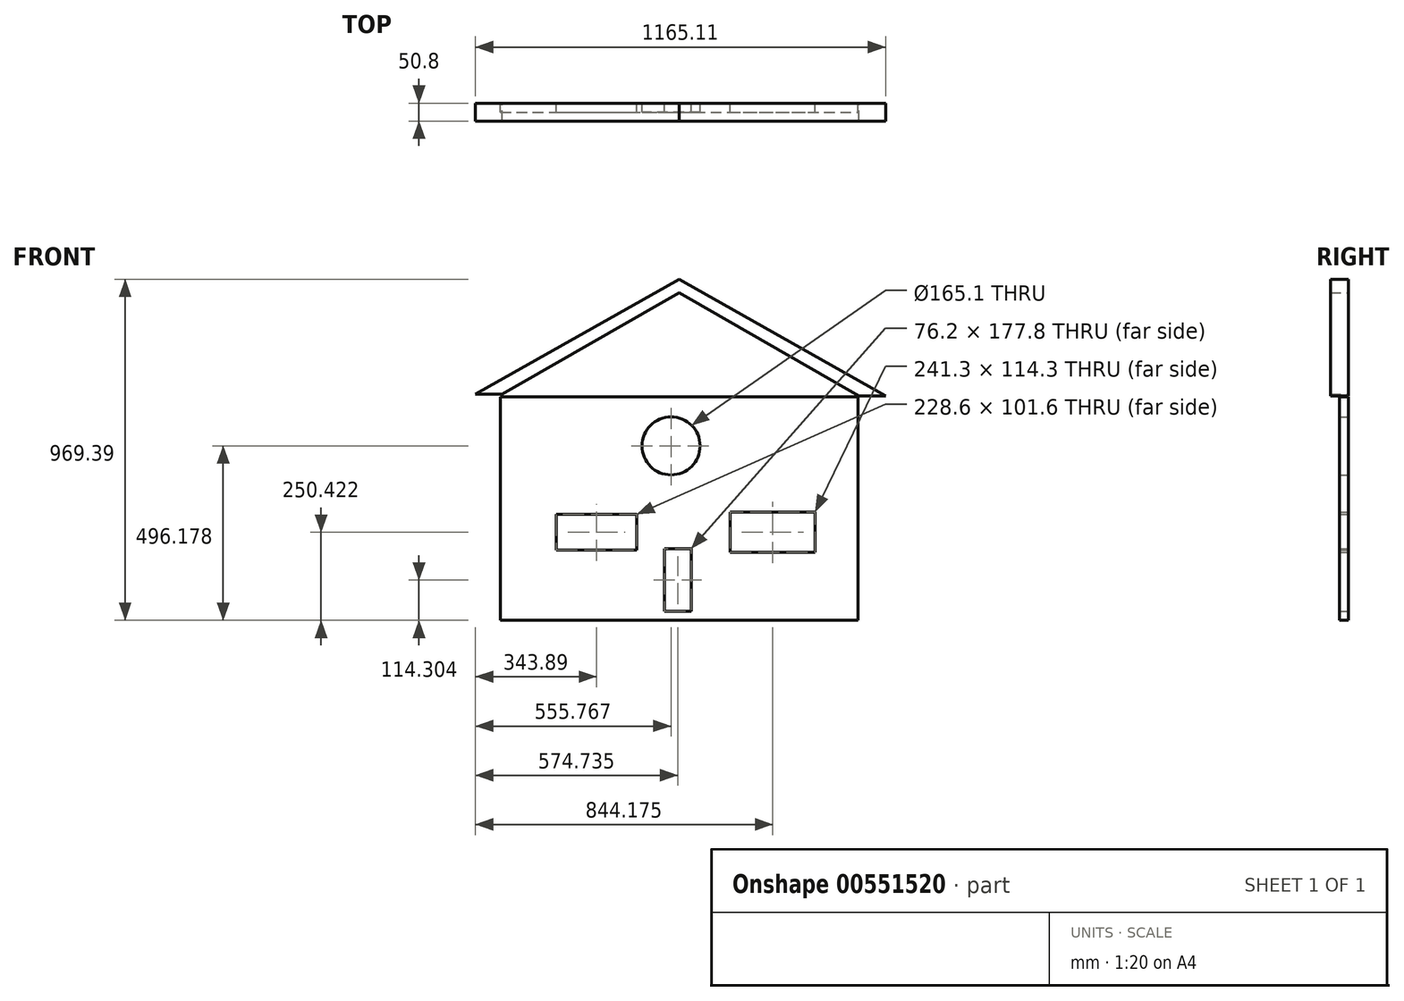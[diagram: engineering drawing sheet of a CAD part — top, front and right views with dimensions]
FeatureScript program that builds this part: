
annotation { "Feature Type Name" : "Feature", "Feature Type Description" : "" }
export const myFeature = defineFeature(function(context is Context, id is Id, definition is map)
    precondition{}
    {
        {
            var Q0;
            Q0=qCreatedBy(makeId("Front.planeOp"),FACE);
            var sketch = newSketch(context, id + "F0", { "sketchPlane" : qUnion([Q0])});
            skLineSegment(sketch, "E0", {"start": v(-620.3, -141.94) * mm, "end": v(-112.3, -141.94) * mm});
            skLineSegment(sketch, "E1", {"start": v(-112.3, -141.94) * mm, "end": v(395.7, -141.94) * mm});
            skLineSegment(sketch, "E2", {"start": v(-112.3, -99.65) * mm, "end": v(-112.3, 154.35) * mm, "construction": true});
            skLineSegment(sketch, "E3", {"start": v(-614.94, -133.46) * mm, "end": v(-112.3, 154.35) * mm});
            skLineSegment(sketch, "E4", {"start": v(397.77, -138.3) * mm, "end": v(-112.3, 154.35) * mm});
            skLineSegment(sketch, "E5", {"start": v(397.77, -138.3) * mm, "end": v(473.97, -138.3) * mm});
            skLineSegment(sketch, "E6", {"start": v(-614.94, -133.46) * mm, "end": v(-691.14, -133.46) * mm});
            skLineSegment(sketch, "E7", {"start": v(-112.3, 154.35) * mm, "end": v(-112.3, 192.45) * mm});
            skLineSegment(sketch, "E8", {"start": v(-691.14, -133.46) * mm, "end": v(-112.3, 192.45) * mm});
            skLineSegment(sketch, "E9", {"start": v(473.97, -138.3) * mm, "end": v(-112.3, 192.45) * mm});
            skLineSegment(sketch, "E10", {"start": v(-620.3, -141.94) * mm, "end": v(-620.3, -751.54) * mm});
            skLineSegment(sketch, "E11", {"start": v(-620.3, -751.54) * mm, "end": v(395.7, -751.54) * mm});
            skLineSegment(sketch, "E12", {"start": v(395.7, -751.54) * mm, "end": v(395.7, -141.94) * mm});
            skLineSegment(sketch, "E13", {"start": v(-620.3, -751.54) * mm, "end": v(-620.3, -776.94) * mm});
            skLineSegment(sketch, "E14", {"start": v(395.7, -751.54) * mm, "end": v(395.7, -776.94) * mm});
            skLineSegment(sketch, "E15", {"start": v(-620.3, -776.94) * mm, "end": v(395.7, -776.94) * mm});
            skLineSegment(sketch, "E16", {"start": v(-154.5, -751.54) * mm, "end": v(-154.5, -573.74) * mm});
            skLineSegment(sketch, "E17", {"start": v(-154.5, -573.74) * mm, "end": v(-78.3, -573.74) * mm});
            skLineSegment(sketch, "E18", {"start": v(-78.3, -573.74) * mm, "end": v(-78.3, -751.54) * mm});
            skLineSegment(sketch, "E19.bottom", {"start": v(-461.55, -475.72) * mm, "end": v(-232.95, -475.72) * mm});
            skLineSegment(sketch, "E19.top", {"start": v(-461.55, -577.32) * mm, "end": v(-232.95, -577.32) * mm});
            skLineSegment(sketch, "E19.left", {"start": v(-461.55, -475.72) * mm, "end": v(-461.55, -577.32) * mm});
            skLineSegment(sketch, "E19.right", {"start": v(-232.95, -475.72) * mm, "end": v(-232.95, -577.32) * mm});
            skLineSegment(sketch, "E20.bottom", {"start": v(38.73, -475.72) * mm, "end": v(267.33, -475.72) * mm});
            skLineSegment(sketch, "E20.top", {"start": v(38.73, -577.32) * mm, "end": v(267.33, -577.32) * mm});
            skLineSegment(sketch, "E20.left", {"start": v(38.73, -475.72) * mm, "end": v(38.73, -577.32) * mm});
            skLineSegment(sketch, "E20.right", {"start": v(267.33, -475.72) * mm, "end": v(267.33, -577.32) * mm});
            skCircle(sketch, "E21", {"center": v(-135.37, -280.76) * mm, "radius": 76.2 * mm});
            skCircle(sketch, "E22.0", {"center": v(-135.37, -280.76) * mm, "radius": 82.55 * mm});
            skLineSegment(sketch, "E23.0", {"start": v(-457.53, -479.74) * mm, "end": v(-236.97, -479.74) * mm});
            skLineSegment(sketch, "E23.1", {"start": v(-457.53, -479.74) * mm, "end": v(-457.53, -573.3) * mm});
            skLineSegment(sketch, "E23.2", {"start": v(-457.53, -573.3) * mm, "end": v(-236.97, -573.3) * mm});
            skLineSegment(sketch, "E23.3", {"start": v(-236.97, -479.74) * mm, "end": v(-236.97, -573.3) * mm});
            skLineSegment(sketch, "E24.0", {"start": v(32.38, -583.67) * mm, "end": v(273.68, -583.67) * mm});
            skLineSegment(sketch, "E24.1", {"start": v(32.38, -469.37) * mm, "end": v(32.38, -583.67) * mm});
            skLineSegment(sketch, "E24.2", {"start": v(32.38, -469.37) * mm, "end": v(273.68, -469.37) * mm});
            skLineSegment(sketch, "E24.3", {"start": v(273.68, -469.37) * mm, "end": v(273.68, -583.67) * mm});
            skSolve(sketch);
        }
        {
            var Q0;
            Q0=makeQuery(id+"F0.imprint","IMPRINT",FACE,{"disambiguationData":[TD([[makeQuery(id+"F0.imprint","IMPRINT",EDGE,{"derivedFrom":sQuery(id+"F0.wireOp",EDGE,"E3")}),1.0]])]});
            var Q1;
            Q1=makeQuery(id+"F0.imprint","IMPRINT",FACE,{"disambiguationData":[TD([[makeQuery(id+"F0.imprint","IMPRINT",EDGE,{"derivedFrom":sQuery(id+"F0.wireOp",EDGE,"E4")}),-1.0]])]});
            extrude(context, id + "F1", {"entities" : qUnion([Q0, Q1]), "depth" : 25.4 * mm, "offsetDistance" : 25.4 * mm});
        }
        {
            var Q0;
            Q0 = qSketchRegion(id + "F0", true);
            var Q1;
            Q1=makeQuery(id+"F1.opExtrude","CAP_FACE",FACE,{"disambiguationData":[OSD([sQuery(id+"F0.wireOp",EDGE,"E3"),sQuery(id+"F0.wireOp",EDGE,"E4"),sQuery(id+"F0.wireOp",EDGE,"E5"),sQuery(id+"F0.wireOp",EDGE,"E6"),sQuery(id+"F0.wireOp",EDGE,"E8"),sQuery(id+"F0.wireOp",EDGE,"E9")])],"isStart":false});
            extrude(context, id + "F2", {"entities" : qUnion([Q0, Q1]), "operationType" : NewBodyOperationType.ADD, "depth" : 25.4 * mm, "offsetDistance" : 25.4 * mm});
        }
    });
